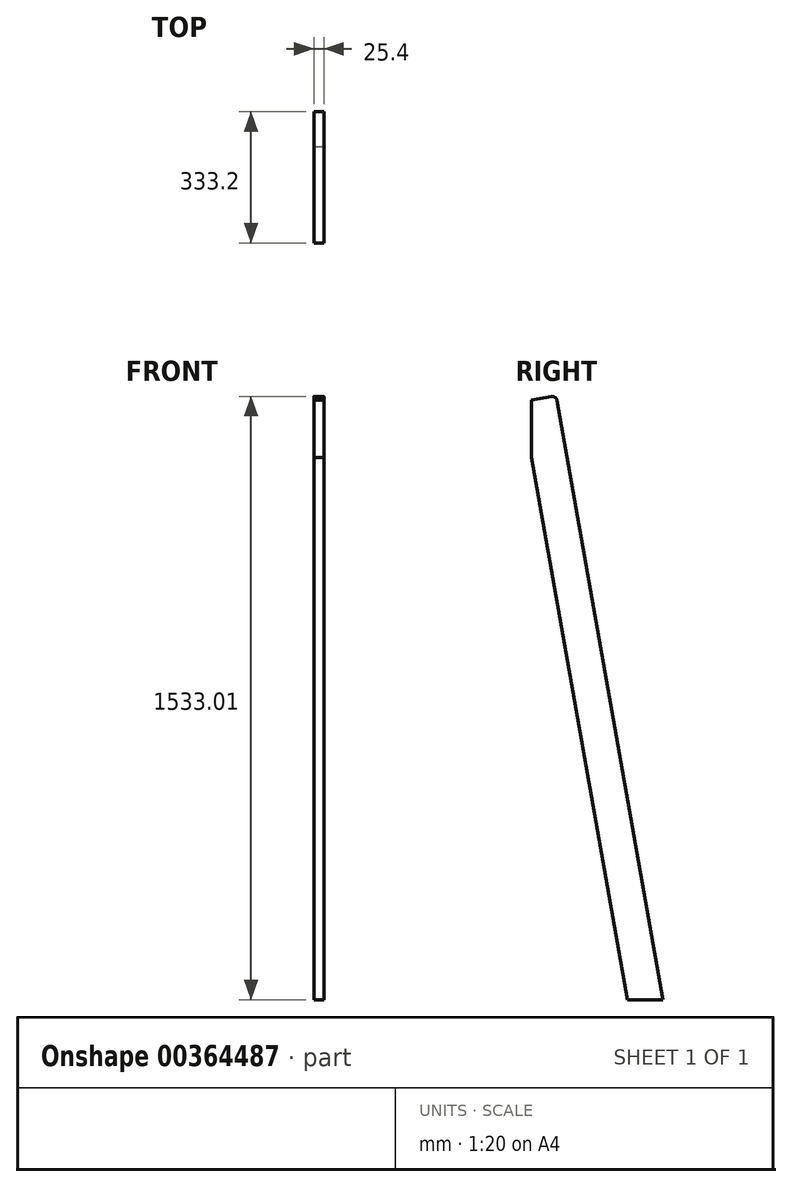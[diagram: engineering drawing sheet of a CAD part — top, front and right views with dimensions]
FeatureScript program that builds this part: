
annotation { "Feature Type Name" : "Feature", "Feature Type Description" : "" }
export const myFeature = defineFeature(function(context is Context, id is Id, definition is map)
    precondition{}
    {
        {
            var Q0;
            Q0=qCreatedBy(makeId("Right.planeOp"),FACE);
            var sketch = newSketch(context, id + "F0", { "sketchPlane" : qUnion([Q0])});
            skLineSegment(sketch, "E0", {"start": v(0, 1377.73) * mm, "end": v(242.93, 0) * mm});
            skLineSegment(sketch, "E1", {"start": v(64.74, 1522.52) * mm, "end": v(333.2, 0) * mm});
            skLineSegment(sketch, "E2", {"start": v(242.93, 0) * mm, "end": v(333.2, 0) * mm});
            skLineSegment(sketch, "E3", {"start": v(0, 1524) * mm, "end": v(50.03, 1532.82) * mm});
            skLineSegment(sketch, "E4", {"start": v(0, 1524) * mm, "end": v(0, 1377.73) * mm});
            skPoint(sketch, "E5.visualSharp", {"position": v(62.54, 1535.03) * mm});
            skArc(sketch, "E5.filletArc", {"start": v(64.74, 1522.52) * mm, "mid": v(59.52, 1530.72) * mm, "end": v(50.03, 1532.82) * mm});
            skSolve(sketch);
        }
        {
            var Q0;
            Q0=qSketchRegion(id+"F0",true);
            extrude(context, id + "F1", {"entities" : qUnion([Q0]), "depth" : 25.4 * mm});
        }
    });
